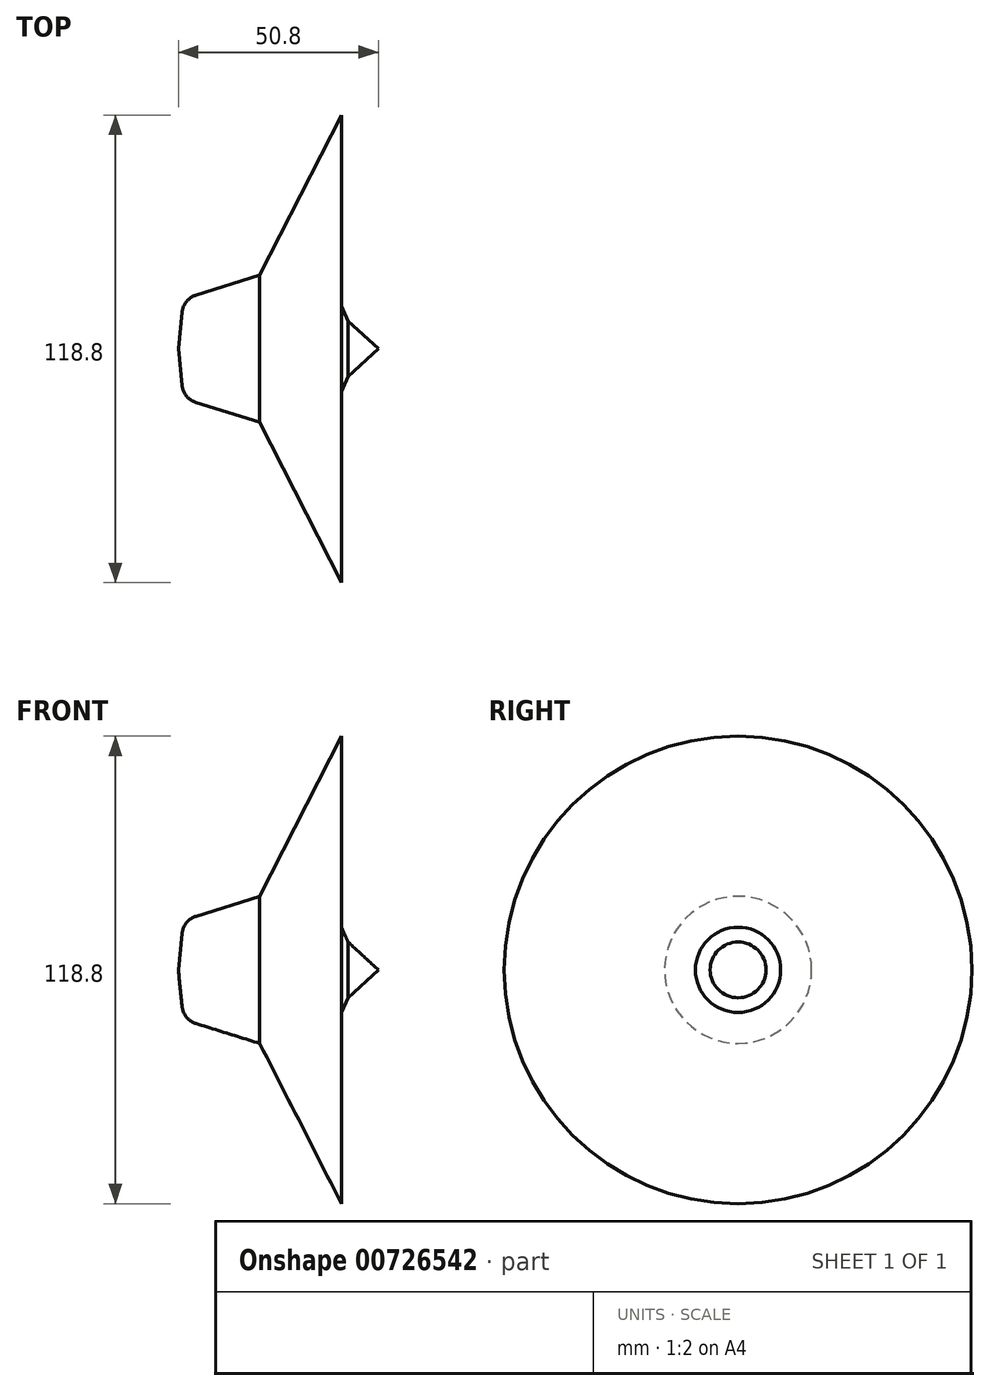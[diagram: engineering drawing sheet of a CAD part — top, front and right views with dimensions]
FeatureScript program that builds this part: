
annotation { "Feature Type Name" : "Feature", "Feature Type Description" : "" }
export const myFeature = defineFeature(function(context is Context, id is Id, definition is map)
    precondition{}
    {
        {
            var Q0;
            Q0=qCreatedBy(makeId("Front.planeOp"),FACE);
            var sketch = newSketch(context, id + "F0", { "sketchPlane" : qUnion([Q0])});
            skLineSegment(sketch, "E0", {"start": v(-49.53, 12.64) * mm, "end": v(-50.8, 0) * mm});
            skLineSegment(sketch, "E1", {"start": v(-30.13, 18.68) * mm, "end": v(-9.34, 59.4) * mm});
            skLineSegment(sketch, "E2", {"start": v(-9.34, 59.4) * mm, "end": v(-9.34, 8.6) * mm});
            skLineSegment(sketch, "E3", {"start": v(-9.34, 8.6) * mm, "end": v(0, 0) * mm});
            skLineSegment(sketch, "E4", {"start": v(0, 0) * mm, "end": v(-50.8, 0) * mm});
            skLineSegment(sketch, "E5", {"start": v(-49.53, 12.64) * mm, "end": v(-30.13, 18.68) * mm});
            skSolve(sketch);
        }
        {
            var Q0;
            Q0=makeQuery(id+"F0.imprint","IMPRINT",FACE,{"disambiguationData":[TD([[makeQuery(id+"F0.imprint","IMPRINT",EDGE,{"derivedFrom":sQuery(id+"F0.wireOp",EDGE,"E0")}),1.0]])]});
            var Q1;
            Q1=sQuery(id+"F0.wireOp",EDGE,"E4");
            revolve(context, id + "F1", {"surfaceOperationType" : NewSurfaceOperationType.NEW, "entities" : qUnion([Q0]), "axis" : qUnion([Q1]), "revolveType" : RevolveType.FULL});
        }
        {
            var Q0;
            Q0=makeQuery(id+"F1.opRevolve","SWEPT_FACE",FACE,{"disambiguationData":[OSD([sQuery(id+"F0.wireOp",EDGE,"E3")])]});
            chamfer(context, id + "F2", {"entities" : qUnion([Q0]), "width" : 5.08 * mm, "tangentPropagation" : true});
        }
        {
            var Q0;
            Q0=makeQuery(id+"F1.opRevolve","SWEPT_FACE",FACE,{"disambiguationData":[OSD([sQuery(id+"F0.wireOp",EDGE,"E0")])]});
            fillet(context, id + "F3", {"entities" : qUnion([Q0]), "radius" : 5.08 * mm, "tangentPropagation" : true, "allowEdgeOverflow" : false});
        }
    });
